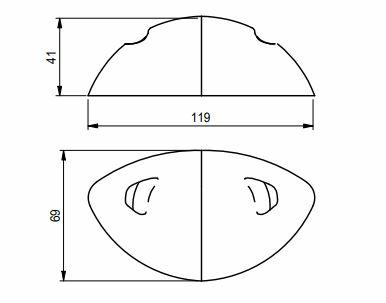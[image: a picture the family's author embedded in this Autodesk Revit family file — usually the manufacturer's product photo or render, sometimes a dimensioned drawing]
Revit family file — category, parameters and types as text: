
# Revit family: R-MBD-493
name_source: partatom
category: Portes
units: mm (PartAtom-declared; Revit-internal decimal feet)

## family parameters
Couper avec des vides une fois chargée = Non
Hôte = Mur
Partagée = Non
Repère de localisation dans la pièce = Oui
Toujours verticalement = Oui

## types (1)
- MBD-493
    1 Vantail = Non
    2 Vantaux = Oui
    A.E.V = non
    Acoustique = non
    Anti-Effraction = non
    Certification = D.A.S. Mode 2 certifié NF
    Code_MAJ = 2303130305MBD493
    Coloris_Chants = BER
    Coloris_Dormant = Hêtre
    Coloris_Face_Cote_Oppose_Ouverture = Prépeint
    Coloris_Face_Cote_Ouverture = Prépeint
    Construction analytique = <Aucun>
    DAS = Oui
    DC Larg Feuillure = 12 mm  [stored 0.0393701 ft]
    DC Pivot Vantail = 60 mm  [stored 0.19685 ft]
    Description = Bloc-porte bois D.A.S. 2 vantaux SP51 avec pivots linteaux motorisés encastrés, double action / va-et-vient, EI60, D.A.S. certifié NF, sur huisserie bois sans montant sans fileur
    Définir les propriétés thermiques par = Type schématique
    Ep Profil Pose Tunnel = 118 mm
    Ep Strat Vantail = 1 mm  [stored 0.00328084 ft]
    Ep Vantail = 51 mm  [stored 0.167323 ft]
    Epaisseur_Rainure à brique = 8 mm  [stored 0.0262467 ft]
    Fabricant = MALERBA
    Fiche_Produit = MBD-493
    Fileur = Non
    Hauteur_Tableau = 2125 mm
    Hauteur_Vantaux_Souhaitée = 2040 mm  [stored 6.69291 ft]
    Jeu_1 = 0 mm  [stored 0 ft]
    Jeu_2 = 0 mm  [stored 0 ft]
    Jeu_Côté_Articulation_Vantail = 8 mm  [stored 0.0262467 ft]
    Jeu_Côté_Fermeture_Vantail = 8 mm  [stored 0.0262467 ft]
    Jeu_Haut = 3 mm  [stored 0.00984252 ft]
    Larg Profil = 58 mm  [stored 0.190289 ft]
    Larg Profil Avec Fileur = 20 mm  [stored 0.0656168 ft]
    Larg Profil Trav = 76 mm  [stored 0.249344 ft]
    Largeur = 0 mm  [stored 0 ft]
    Largeur_Vantail_Semi_Fixe_Souhaitée = 930 mm  [stored 3.05118 ft]
    Largeur_Vantail_Service_Souhaitée = 930 mm  [stored 3.05118 ft]
    Mat APD = Caoutchouc noir
    Mat Parclose = BER 2
    Mat Parclose Métal = Peinture Laquée PMT - Blanc Pur - RAL 9010
    Materiaux_Dominant = Bois
    Modèle = Va et vient
    Montant_VV = Oui
    Note d'identification = 2V EI60/SP51 DAS - LINTEAU MOTORISE - SANS MONTANT SANS FILEUR
    Pivot linteau motorisé = Oui
    Profondeur_Rainure à brique = 5 mm  [stored 0.0164042 ft]
    Reference_Commerciale = 2V SP51/DA LINTEAU OP
    Resistance_Feu = EI30
    Sans_Montants = Non
    Sens_Feu = Recto / Verso
    Thermique (W/m2.°K) = 0
    URL = https://www.malerba.fr
    X_Axe Pivot = 114 mm  [stored 0.374016 ft]
    X_DC seuil = 9 mm  [stored 0.0295276 ft]
    X_Inv_DC Larg Feuillure_1V Montant = 0 mm  [stored 0 ft]

note: [stored X ft] marks values corroborated as IEEE doubles in the binary element streams (Revit-internal decimal feet)

## geometry (parser evidence)
native form markers: Blend x14
no freeform markers — native parametric forms only
